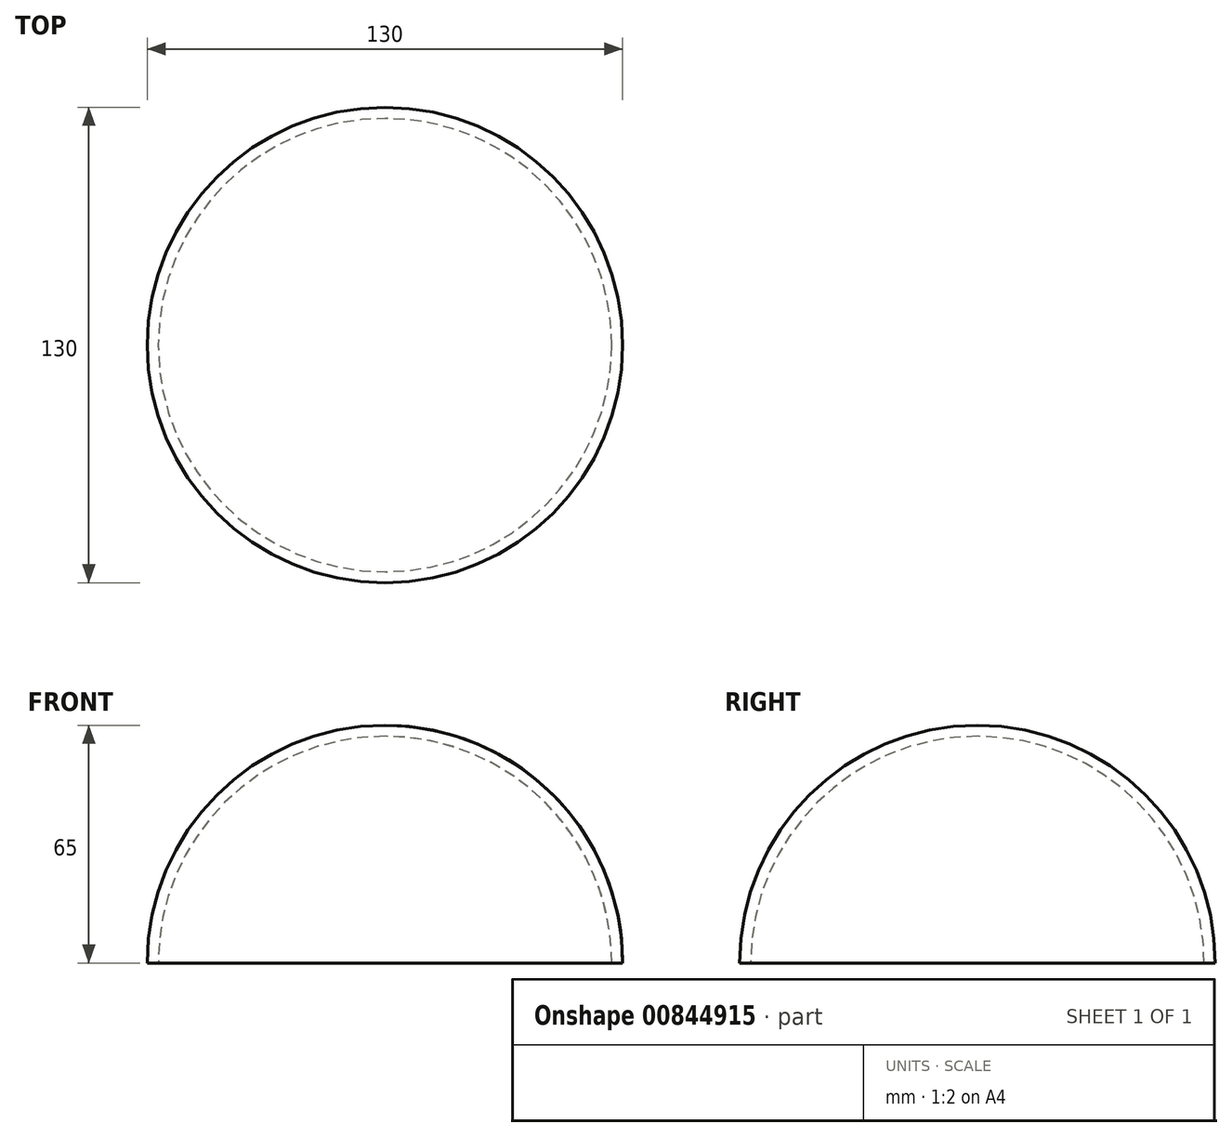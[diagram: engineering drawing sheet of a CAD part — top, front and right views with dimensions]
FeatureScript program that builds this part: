
annotation { "Feature Type Name" : "Feature", "Feature Type Description" : "" }
export const myFeature = defineFeature(function(context is Context, id is Id, definition is map)
    precondition{}
    {
        {
            var Q0;
            Q0=qCreatedBy(makeId("Front.planeOp"),FACE);
            var sketch = newSketch(context, id + "F0", { "sketchPlane" : qUnion([Q0])});
            skArc(sketch, "E0", {"start": v(65, 0) * mm, "mid": v(45.96, 45.96) * mm, "end": v(0, 65) * mm});
            skArc(sketch, "E1", {"start": v(62, 0) * mm, "mid": v(43.84, 43.84) * mm, "end": v(0, 62) * mm});
            skLineSegment(sketch, "E2", {"start": v(62, 0) * mm, "end": v(65, 0) * mm});
            skLineSegment(sketch, "E3", {"start": v(0, 65) * mm, "end": v(0, 62) * mm});
            skLineSegment(sketch, "E4", {"start": v(0, 107.63) * mm, "end": v(0, -72.9) * mm});
            skSolve(sketch);
        }
        {
            var Q0;
            Q0=makeQuery(id+"F0.imprint","IMPRINT",FACE,{"disambiguationData":[TD([[makeQuery(id+"F0.imprint","IMPRINT",EDGE,{"derivedFrom":sQuery(id+"F0.wireOp",EDGE,"E0")}),1.0]])]});
            var Q1;
            Q1=sQuery(id+"F0.wireOp",EDGE,"E4");
            revolve(context, id + "F1", {"surfaceOperationType" : NewSurfaceOperationType.NEW, "entities" : qUnion([Q0]), "axis" : qUnion([Q1]), "revolveType" : RevolveType.FULL});
        }
    });
